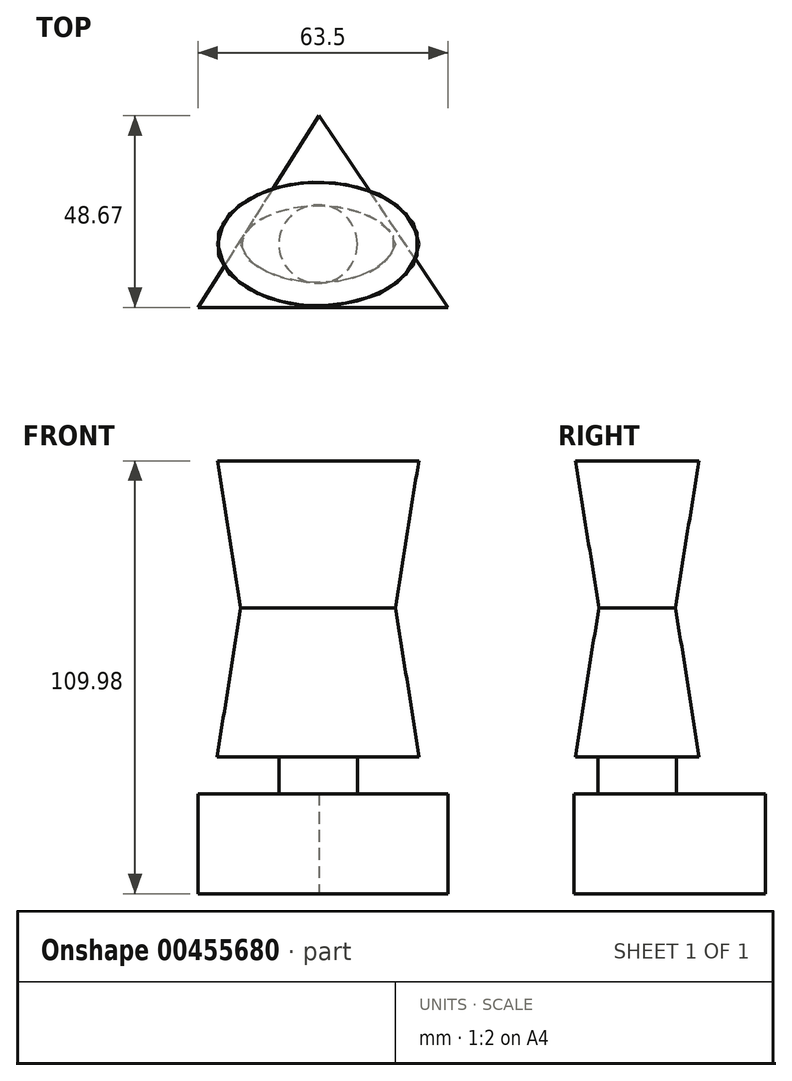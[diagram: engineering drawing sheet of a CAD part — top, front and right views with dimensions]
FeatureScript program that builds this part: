
annotation { "Feature Type Name" : "Feature", "Feature Type Description" : "" }
export const myFeature = defineFeature(function(context is Context, id is Id, definition is map)
    precondition{}
    {
        {
            var Q0;
            Q0=qCreatedBy(makeId("Top.planeOp"),FACE);
            var sketch = newSketch(context, id + "F0", { "sketchPlane" : qUnion([Q0])});
            skLineSegment(sketch, "E0", {"start": v(0, 0) * mm, "end": v(63.5, 0) * mm});
            skLineSegment(sketch, "E1", {"start": v(63.5, 0) * mm, "end": v(30.73, 48.67) * mm});
            skLineSegment(sketch, "E2", {"start": v(30.73, 48.67) * mm, "end": v(0, 0) * mm});
            skSolve(sketch);
        }
        {
            var Q0;
            Q0=makeQuery(id+"F0.imprint","IMPRINT",FACE,{"disambiguationData":[TD([[makeQuery(id+"F0.imprint","IMPRINT",EDGE,{"derivedFrom":sQuery(id+"F0.wireOp",EDGE,"E0")}),1.0]])]});
            extrude(context, id + "F1", {"entities" : qUnion([Q0]), "depth" : 25.4 * mm});
        }
        {
            var Q0;
            Q0=makeQuery(id+"F1.opExtrude","CAP_FACE",FACE,{"disambiguationData":[OSD([sQuery(id+"F0.wireOp",EDGE,"E0"),sQuery(id+"F0.wireOp",EDGE,"E1"),sQuery(id+"F0.wireOp",EDGE,"E2")])],"isStart":false});
            var sketch = newSketch(context, id + "F2", { "sketchPlane" : qUnion([Q0])});
            skCircle(sketch, "E3", {"center": v(30.52, 16.08) * mm, "radius": 9.95 * mm});
            skSolve(sketch);
        }
        {
            var Q0;
            Q0=makeQuery(id+"F2.imprint","IMPRINT",FACE,{"disambiguationData":[TD([[makeQuery(id+"F2.imprint","IMPRINT",EDGE,{"derivedFrom":sQuery(id+"F2.wireOp",EDGE,"E3")}),1.0]])]});
            extrude(context, id + "F3", {"entities" : qUnion([Q0]), "operationType" : NewBodyOperationType.ADD, "depth" : 9.4 * mm});
        }
        {
            var Q0;
            Q0=makeQuery(id+"F3.opExtrude","CAP_FACE",FACE,{"disambiguationData":[OSD([sQuery(id+"F2.wireOp",EDGE,"E3")])],"isStart":false});
            var sketch = newSketch(context, id + "F4", { "sketchPlane" : qUnion([Q0])});
            skEllipse(sketch, "E4", {"center": v(30.52, 16.08) * mm, "majorRadius": 25.65 * mm, "minorRadius": 15.74 * mm, "majorAxis": v(-1, 0)});
            skSolve(sketch);
        }
        {
            var Q0;
            Q0=makeQuery(id+"F4.imprint","IMPRINT",FACE,{"disambiguationData":[TD([[makeQuery(id+"F4.imprint","IMPRINT",EDGE,{"derivedFrom":sQuery(id+"F4.wireOp",EDGE,"E4")}),1.0]])]});
            var Q1;
            Q1=makeQuery(id+"F4.imprint","IMPRINT",FACE,{"disambiguationData":[TD([[makeQuery(id+"F4.imprint","IMPRINT",EDGE,{"derivedFrom":makeQuery(id+"F3.opExtrude","CAP_EDGE",EDGE,{"disambiguationData":[OSD([sQuery(id+"F2.wireOp",EDGE,"E3")])],"isStart":false})}),1.0]])]});
            extrude(context, id + "F5", {"entities" : qUnion([Q0, Q1]), "operationType" : NewBodyOperationType.ADD, "depth" : 37.85 * mm, "hasDraft" : true, "draftAngle" : 9 * degree, "draftPullDirection" : true});
        }
        {
            var Q0;
            Q0=makeQuery(id+"F5.opExtrude","CAP_FACE",FACE,{"disambiguationData":[OSD([sQuery(id+"F4.wireOp",EDGE,"E4")])],"isStart":false});
            extrude(context, id + "F6", {"entities" : qUnion([Q0]), "depth" : 37.34 * mm, "hasDraft" : true, "draftAngle" : 9 * degree});
        }
    });
